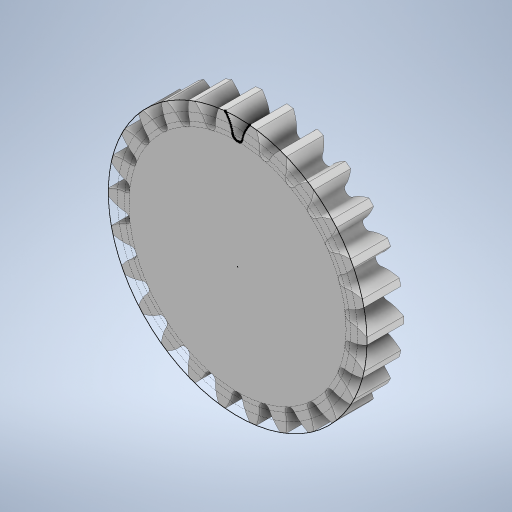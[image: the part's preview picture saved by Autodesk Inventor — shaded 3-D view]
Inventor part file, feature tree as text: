
AUTODESK INVENTOR PART (.ipt)
format: ipt  version: 2024 (Build 280153000, 153)  size: 427,520 bytes
history: native  units: mm
features: extrude x2, pattern_circular x1
ambient origin geometry x8: Origin, YZ Plane, XZ Plane, XY Plane, X Axis, Y Axis, Z Axis, Center Point
bodies: Solid1 (feature_tree)
feature tree (3):
  extrude  "Extrusion1"  Depth=20.0mm
  extrude  "Extrusion2"  TaperAngle=0.0deg  [1 undecoded]
  pattern_circular  "Circular Pattern1"  Count=3  [1 undecoded]
note: 2 required parameter values undecoded (feature->parameter linkage not recoverable at this tier; creation-order binding heuristic only, values carry confidence <= 0.55)
